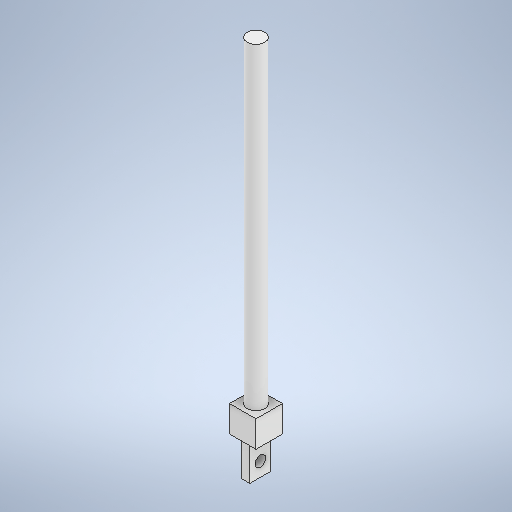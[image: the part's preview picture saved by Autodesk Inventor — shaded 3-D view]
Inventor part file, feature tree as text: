
AUTODESK INVENTOR PART (.ipt)
format: ipt  version: 2025.3 (Build 293356000, 356)  size: 269,824 bytes
history: native  units: mm
features: extrude x4, sketch x4, other x1
ambient origin geometry x8: Origin, YZ Plane, XZ Plane, XY Plane, X Axis, Y Axis, Z Axis, Center Point
bodies: Body1 (feature_tree)
feature tree (9):
  other  "pendulum"
  extrude  "Extrusión2"  Depth=180.0mm TaperAngle=0.0deg
  extrude  "Extrusión3"  Depth=15.0mm
  extrude  "Extrusión4"  Depth=5.0mm
  extrude  "Extrusión5"  Depth=20.0mm TaperAngle=0.0deg
  sketch  "Boceto3"  dims[d21=10.0mm d22=180.0mm d23=0.0mm]
  sketch  "Boceto4"  dims[d24=15.0mm d25=15.0mm]
  sketch  "Boceto5"  dims[d26=15.0mm d27=0.0mm d28=5.0mm]
  sketch  "Boceto6"  dims[d29=12.0mm d30=20.0mm d31=0.0mm d32=8.0mm d33=6.0mm d34=20.0mm d35=0.0mm d5=0.5mm d6=0.872665mm d7=0.5mm d8=0.872665mm d9=0.0mm d10=0.0mm d11=0.0mm d12=0.0mm d36=0.0mm d37=0.0mm d38=0.0mm d39=0.0mm]
